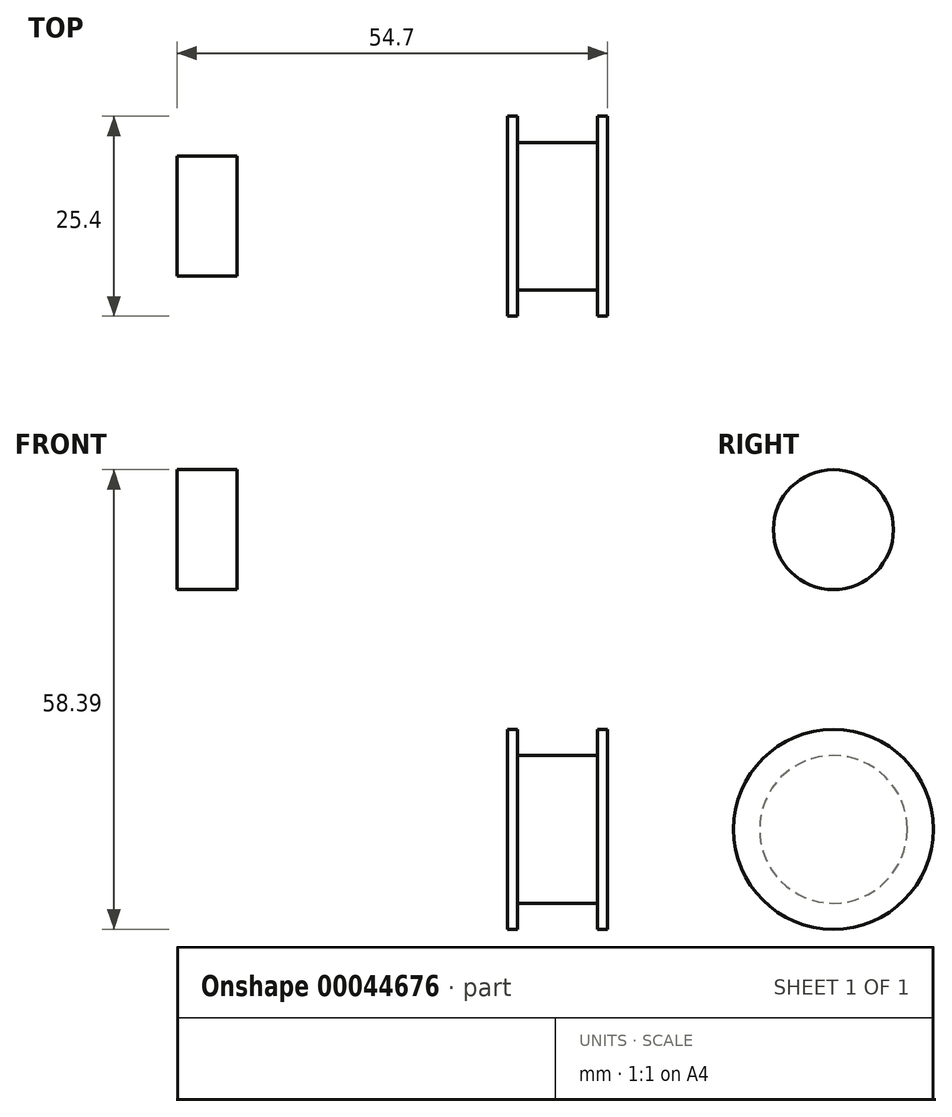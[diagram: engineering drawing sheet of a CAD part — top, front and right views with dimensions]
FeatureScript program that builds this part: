
annotation { "Feature Type Name" : "Feature", "Feature Type Description" : "" }
export const myFeature = defineFeature(function(context is Context, id is Id, definition is map)
    precondition{}
    {
        {
            var Q0;
            Q0=qCreatedBy(makeId("Front.planeOp"),FACE);
            var sketch = newSketch(context, id + "F0", { "sketchPlane" : qUnion([Q0])});
            skLineSegment(sketch, "E0.bottom", {"start": v(-13.92, 14.62) * mm, "end": v(-12.65, 14.62) * mm});
            skLineSegment(sketch, "E0.top", {"start": v(-13.92, 1.92) * mm, "end": v(-1.22, 1.92) * mm});
            skLineSegment(sketch, "E0.left", {"start": v(-13.92, 14.62) * mm, "end": v(-13.92, 1.92) * mm});
            skLineSegment(sketch, "E0.right", {"start": v(-1.22, 14.62) * mm, "end": v(-1.22, 1.92) * mm});
            skLineSegment(sketch, "E1.trimOffspring", {"start": v(-2.49, 14.62) * mm, "end": v(-1.22, 14.62) * mm});
            skPoint(sketch, "E2.center.orphan", {"position": v(-7.57, 14.62) * mm});
            skLineSegment(sketch, "E3", {"start": v(-12.65, 14.62) * mm, "end": v(-12.65, 11.3) * mm});
            skLineSegment(sketch, "E4", {"start": v(-12.65, 11.3) * mm, "end": v(-2.49, 11.3) * mm});
            skLineSegment(sketch, "E5", {"start": v(-2.49, 11.3) * mm, "end": v(-2.49, 14.62) * mm});
            skSolve(sketch);
        }
        {
            var Q0;
            Q0=makeQuery(id+"F0.imprint","IMPRINT",FACE,{"disambiguationData":[TD([[makeQuery(id+"F0.imprint","IMPRINT",EDGE,{"derivedFrom":sQuery(id+"F0.wireOp",EDGE,"E0.bottom")}),-1.0]])]});
            var Q1;
            Q1=sQuery(id+"F0.wireOp",EDGE,"E0.top");
            revolve(context, id + "F1", {"entities" : qUnion([Q0]), "axis" : qUnion([Q1]), "revolveType" : RevolveType.FULL});
        }
        {
            var Q0;
            Q0=qCreatedBy(makeId("Front.planeOp"),FACE);
            var sketch = newSketch(context, id + "F2", { "sketchPlane" : qUnion([Q0])});
            skLineSegment(sketch, "E6.bottom", {"start": v(-55.92, 39.99) * mm, "end": v(-48.3, 39.99) * mm});
            skLineSegment(sketch, "E6.top", {"start": v(-55.92, 32.37) * mm, "end": v(-48.3, 32.37) * mm});
            skLineSegment(sketch, "E6.left", {"start": v(-55.92, 39.99) * mm, "end": v(-55.92, 32.37) * mm});
            skLineSegment(sketch, "E6.right", {"start": v(-48.3, 39.99) * mm, "end": v(-48.3, 32.37) * mm});
            skSolve(sketch);
        }
        {
            var Q0;
            Q0=makeQuery(id+"F2.imprint","IMPRINT",FACE,{"disambiguationData":[TD([[makeQuery(id+"F2.imprint","IMPRINT",EDGE,{"derivedFrom":sQuery(id+"F2.wireOp",EDGE,"E6.bottom")}),-1.0]])]});
            var Q1;
            Q1=sQuery(id+"F2.wireOp",EDGE,"E6.bottom");
            revolve(context, id + "F3", {"entities" : qUnion([Q0]), "axis" : qUnion([Q1]), "revolveType" : RevolveType.FULL});
        }
    });
